# Revit family: Faucet-Wall_Mount-Bath_Spout-KOHLER-Aleo-K-20077IN_1
name_source: partatom
category: Plumbing Fixtures
units: mm (PartAtom-declared; Revit-internal decimal feet)

## family parameters
Cut with Voids When Loaded = No
Host = Face
Maintain Annotation Orientation = No
OmniClass Number = 23.31.11.00
OmniClass Title = Faucets
Part Type = Normal
Room Calculation Point = No
Round Connector Dimension = Use Diameter
Shared = No

## types (5) — shared parameters
ADA Compliant = No
Assembly Code = D2010
CW Connection = No
Cold Water Inlet = Cold Water Inlet
Date Modified = 02/09/2022
Default Elevation = 36"
Drain Included = No
Flow Rate = 0 GPM
HW Connection = Yes
Height = 3 1/8"
Hot Water Inlet = Tempered Water Inlet
Length = 6 1/4"
Manufacturer = KOHLER Co.
Master Format 2014 = 22 41 39
Master Format 2014 Name = Residential Faucets, Supplies, and Trim
Material = Premium Metal Construction
Pressure = 0.00 psi
Product Name = Aleo
Spout Reach = 6 1/4"
URL = https://www.kohler.co.in
Vent Connection = No
Waste Connection = No
Waste Water Outlet = Waste Water Outlet
WaterSense Certified = No
Width = 2 3/4"

## per-type parameters (varying)
| type | Description | Finish | Model | Product Page URL | Type | With Diverter | Without Diverter |
| With Diverter, CP-Polished Chrome | Bath Spout With Diverter | Kohler-Metal-CP-Polished_Chrome | K-20077IN-CP | https://www.kohler.co.in | 1 | Yes | No |
| With Diverter, BL-Matte Black | Bath Spout With Diverter | Kohler-Metal-BL-Matte_Black | K-20077IN-BL | https://www.kohler.co.in | 2 | Yes | No |
| With Diverter, AF-Vibrant French Gold | Bath Spout With Diverter | Kohler-Metal-AF-Vibrant_French_Gold | K-20077IN-AF | https://www.kohler.co.in | 3 | Yes | No |
| Without Diverter, CP-Polished Chrome | BATH SPOUT | Kohler-Metal-CP-Polished_Chrome | K-20077IN-4-CP |  | 4 | No | Yes |
| Without Diverter, AF-Vibrant French Gold | BATH SPOUT | Kohler-Metal-AF-Vibrant_French_Gold | K-20077IN-4-AF |  | 5 | No | Yes |

## geometry (parser evidence)
native form markers: Sweep x6
no freeform markers — native parametric forms only
